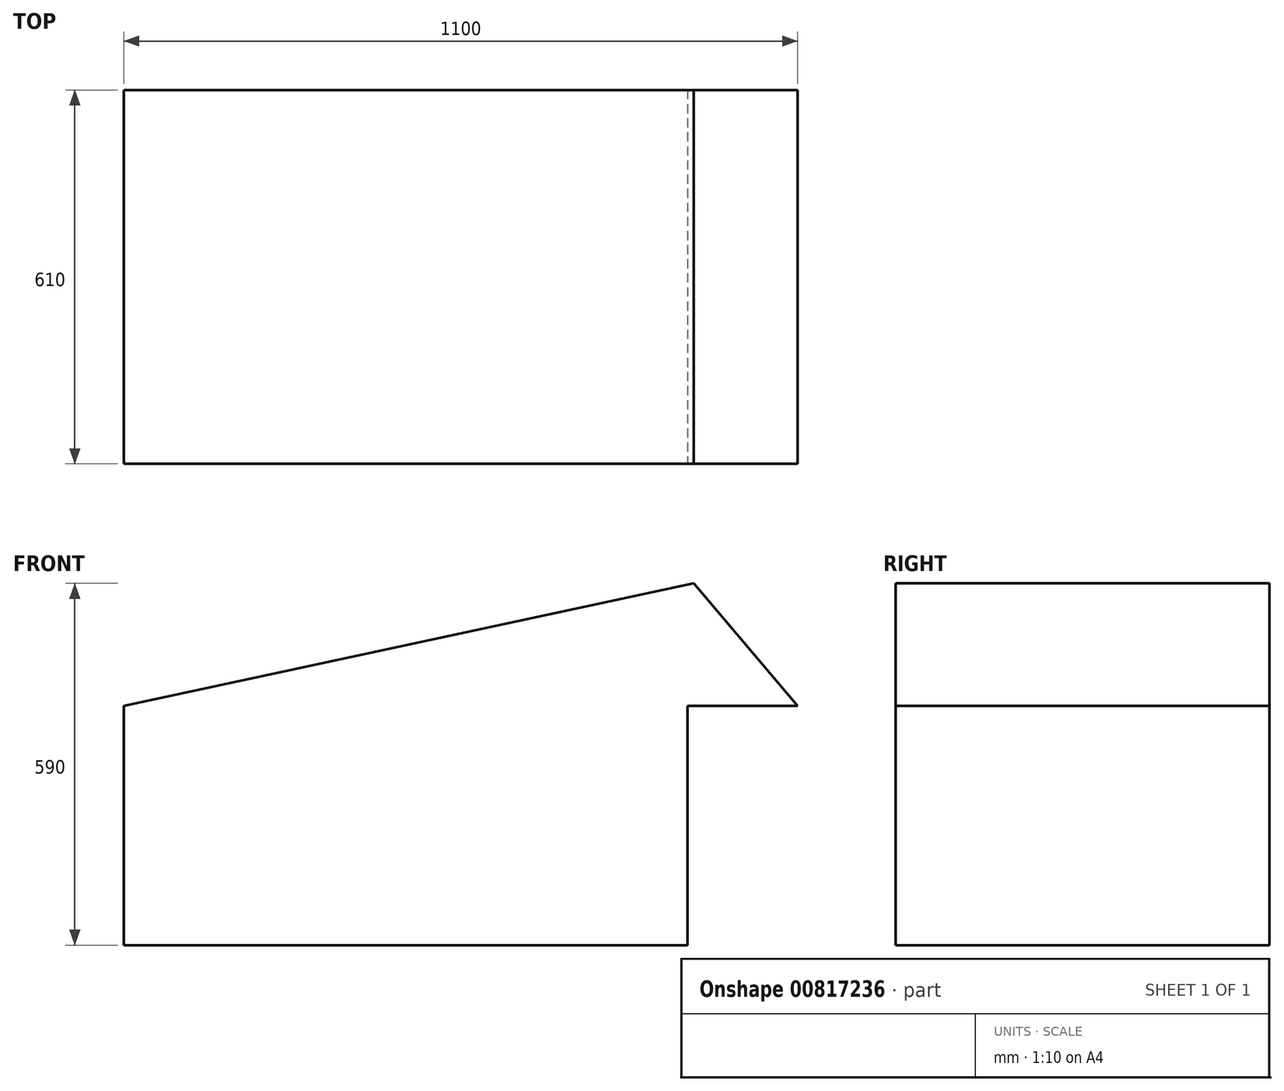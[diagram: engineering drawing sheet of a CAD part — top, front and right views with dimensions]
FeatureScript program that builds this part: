
annotation { "Feature Type Name" : "Feature", "Feature Type Description" : "" }
export const myFeature = defineFeature(function(context is Context, id is Id, definition is map)
    precondition{}
    {
        {
            var Q0;
            Q0=qCreatedBy(makeId("Top.planeOp"),FACE);
            var sketch = newSketch(context, id + "F0", { "sketchPlane" : qUnion([Q0])});
            skLineSegment(sketch, "E0.bottom", {"start": v(550, -305) * mm, "end": v(-550, -305) * mm});
            skLineSegment(sketch, "E0.top", {"start": v(550, 305) * mm, "end": v(-550, 305) * mm});
            skLineSegment(sketch, "E0.left", {"start": v(550, -305) * mm, "end": v(550, 305) * mm});
            skLineSegment(sketch, "E0.right", {"start": v(-550, -305) * mm, "end": v(-550, 305) * mm});
            skPoint(sketch, "E0.middle", {"position": v(0, 0) * mm});
            skSolve(sketch);
        }
        {
            var Q0;
            Q0=makeQuery(id+"F0.imprint","IMPRINT",FACE,{"disambiguationData":[TD([[makeQuery(id+"F0.imprint","IMPRINT",EDGE,{"derivedFrom":sQuery(id+"F0.wireOp",EDGE,"E0.bottom")}),-1.0]])]});
            extrude(context, id + "F1", {"entities" : qUnion([Q0]), "depth" : (390 + 200) * mm, "offsetDistance" : 25 * mm});
        }
        {
            var Q0;
            Q0=makeQuery(id+"F1.opExtrude","SWEPT_FACE",FACE,{"disambiguationData":[OSD([sQuery(id+"F0.wireOp",EDGE,"E0.bottom")])]});
            var sketch = newSketch(context, id + "F2", { "sketchPlane" : qUnion([Q0])});
            skLineSegment(sketch, "E1.bottom", {"start": v(550, 0) * mm, "end": v(370, 0) * mm});
            skLineSegment(sketch, "E1.top", {"start": v(550, 390) * mm, "end": v(370, 390) * mm});
            skLineSegment(sketch, "E1.left", {"start": v(550, 0) * mm, "end": v(550, 390) * mm});
            skLineSegment(sketch, "E1.right", {"start": v(370, 0) * mm, "end": v(370, 390) * mm});
            skLineSegment(sketch, "E2", {"start": v(550, 390) * mm, "end": v(380.14, 590) * mm});
            skLineSegment(sketch, "E3", {"start": v(380.14, 590) * mm, "end": v(-550, 390) * mm});
            skLineSegment(sketch, "E4", {"start": v(-550, 390) * mm, "end": v(-550, 590) * mm});
            skLineSegment(sketch, "E5", {"start": v(-550, 590) * mm, "end": v(380.14, 590) * mm});
            skLineSegment(sketch, "E6", {"start": v(550, 590) * mm, "end": v(550, 390) * mm});
            skSolve(sketch);
        }
        {
            var Q0;
            Q0=makeQuery(id+"F2.imprint","IMPRINT",FACE,{"disambiguationData":[TD([[makeQuery(id+"F2.imprint","IMPRINT",EDGE,{"derivedFrom":sQuery(id+"F2.wireOp",EDGE,"E3")}),-1.0]])]});
            var Q1;
            {var subQ0=sQuery(id+"F2.wireOp",EDGE,"E2");Q1=makeQuery(id+"F2.imprint","IMPRINT",FACE,{"disambiguationData":[TD([[makeQuery(id+"F2.imprint","IMPRINT",EDGE,{"derivedFrom":subQ0}),-1.0]])]});}
            var Q2;
            Q2=makeQuery(id+"F2.imprint","IMPRINT",FACE,{"disambiguationData":[TD([[makeQuery(id+"F2.imprint","IMPRINT",EDGE,{"derivedFrom":sQuery(id+"F2.wireOp",EDGE,"E1.bottom")}),-1.0]])]});
            var Q3;
            Q3=makeQuery(id+"F1.opExtrude","SWEPT_FACE",FACE,{"disambiguationData":[OSD([sQuery(id+"F0.wireOp",EDGE,"E0.top")])]});
            extrude(context, id + "F3", {"entities" : qUnion([Q0, Q1, Q2]), "operationType" : NewBodyOperationType.REMOVE, "endBound" : BoundingType.UP_TO_SURFACE, "oppositeDirection" : true, "depth" : 25 * mm, "endBoundEntityFace" : qUnion([Q3]), "offsetDistance" : 25 * mm});
        }
    });
